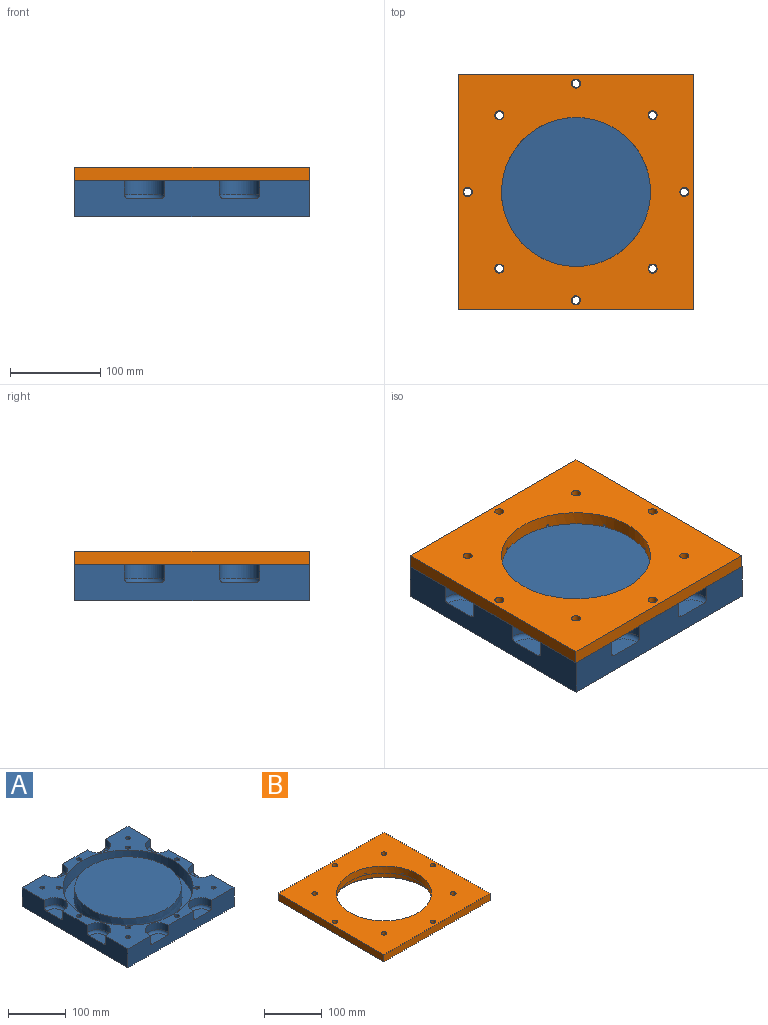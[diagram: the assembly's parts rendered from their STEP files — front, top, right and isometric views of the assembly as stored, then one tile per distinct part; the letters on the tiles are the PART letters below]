
ASSEMBLY  parts=2 mates=1
PART A: 46 faces, bbox 262x262x40 mm
  f0: plane 260x40mm, normal (0,1,0), area 8632.8mm2, adj f1,f15,f16,f17,f34,f35,f36,f37
  f1: plane 260x40mm, normal (-1,0,0), area 8632.8mm2, adj f0,f2,f16,f17,f30,f31,f32,f33
  f2: plane 260x40mm, normal (0,-1,0), area 8632.8mm2, adj f1,f15,f16,f17,f26,f27,f28,f29
  f3: cylinder r=4.3mm len=40mm, axis (0,0,1), area 1080.7mm2, adj f16,f17
  f4: cylinder r=4.3mm len=40mm, axis (0,0,1), area 1080.7mm2, adj f16,f17
  f5: cylinder r=4.3mm len=40mm, axis (0,0,1), area 1080.7mm2, adj f16,f17
  f6: cylinder r=4.3mm len=40mm, axis (0,0,1), area 1080.7mm2, adj f16,f17
  f7: cylinder r=4.3mm len=40mm, axis (0,0,1), area 1080.7mm2, adj f16,f17
  f8: cylinder r=4.3mm len=40mm, axis (0,0,1), area 1080.7mm2, adj f16,f17
  f9: cylinder r=4.3mm len=40mm, axis (0,0,1), area 1080.7mm2, adj f16,f17
  f10: cylinder r=4.3mm len=40mm, axis (0,0,1), area 1080.7mm2, adj f16,f17
  f11: cylinder r=4.3mm len=40mm, axis (0,0,1), area 1080.7mm2, adj f16,f17
  f12: cylinder r=4.3mm len=40mm, axis (0,0,1), area 1080.7mm2, adj f16,f17
  f13: cylinder r=4.3mm len=40mm, axis (0,0,1), area 1080.7mm2, adj f16,f17
  f14: cylinder r=4.3mm len=40mm, axis (0,0,1), area 1080.7mm2, adj f16,f17
  f15: plane 260x40mm, normal (1,0,0), area 8632.8mm2, adj f0,f2,f16,f17,f22,f23,f24,f25
  f16: plane 260x260mm, normal (0,0,-1), area 66902.9mm2, adj f0,f1,f2,f3,f4,f5,f6,f7
  f17: plane 260x260mm, normal (0,0,1), area 19526.4mm2, adj f0,f1,f2,f3,f4,f5,f6,f7
  f18: cone r=92.5mm half-angle=3deg, axis (0,0,-1), area 14652.8mm2, adj f20,f21
  f19: cone r=113mm half-angle=3deg, axis (0,0,1), area 17671.3mm2, adj f17,f20
  f20: plane 223.38x223.38mm, normal (0,0,1), area 11543mm2, adj f18,f19
  f21: plane 185x185mm, normal (0,0,1), area 26880.3mm2, adj f18
  f22: plane 35x20mm, normal (0,0,1), area 568.4mm2, adj f15,f43
  f23: cylinder r=22.5mm len=45mm, axis (0,0,1), area 1135.6mm2, adj f15,f17,f43
  f24: plane 35x20mm, normal (0,0,1), area 568.4mm2, adj f15,f42
  f25: cylinder r=22.5mm len=45mm, axis (0,0,1), area 1135.6mm2, adj f15,f17,f42
  f26: cylinder r=22.5mm len=45mm, axis (0,0,1), area 1135.6mm2, adj f2,f17,f45
  f27: plane 35x20mm, normal (0,0,1), area 568.4mm2, adj f2,f45
  f28: cylinder r=22.5mm len=45mm, axis (0,0,1), area 1135.6mm2, adj f2,f17,f44
  f29: plane 35x20mm, normal (0,0,1), area 568.4mm2, adj f2,f44
  f30: cylinder r=22.5mm len=45mm, axis (0,0,1), area 1135.6mm2, adj f1,f17,f39
  f31: plane 35x20mm, normal (0,0,1), area 568.4mm2, adj f1,f39
  f32: cylinder r=22.5mm len=45mm, axis (0,0,1), area 1135.6mm2, adj f1,f17,f38
  f33: plane 35x20mm, normal (0,0,1), area 568.4mm2, adj f1,f38
  f34: plane 35x20mm, normal (0,0,1), area 568.4mm2, adj f0,f41
  f35: cylinder r=22.5mm len=45mm, axis (0,0,1), area 1135.6mm2, adj f0,f17,f41
  f36: plane 35x20mm, normal (0,0,1), area 568.4mm2, adj f0,f40
  f37: cylinder r=22.5mm len=45mm, axis (0,0,1), area 1135.6mm2, adj f0,f17,f40
  f38: torus R=17.5mm, axis (0,0,1), area 549.8mm2, adj f1,f32,f33
  f39: torus R=17.5mm, axis (0,0,1), area 549.8mm2, adj f1,f30,f31
  f40: torus R=17.5mm, axis (0,0,1), area 549.8mm2, adj f0,f36,f37
  f41: torus R=17.5mm, axis (0,0,1), area 549.8mm2, adj f0,f34,f35
  f42: torus R=17.5mm, axis (0,0,1), area 549.8mm2, adj f15,f24,f25
  f43: torus R=17.5mm, axis (0,0,1), area 549.8mm2, adj f15,f22,f23
  f44: torus R=17.5mm, axis (0,0,1), area 549.8mm2, adj f2,f28,f29
  f45: torus R=17.5mm, axis (0,0,1), area 549.8mm2, adj f2,f26,f27
PART B: 152 faces, bbox 260x260x35 mm
  f0: plane 192.29x192.29mm, normal (0,0,-1), area 1974.4mm2, adj f24,f25,f26,f27,f28,f29,f30,f31
  f1: plane 260x260mm, normal (0,0,-1), area 26588.3mm2, adj f11,f12,f13,f14,f15,f16,f17,f18
  f2: plane 51.92x51.92mm, normal (0,0,-1), area 657.2mm2, adj f9,f36,f57,f61,f100,f101
  f3: plane 68.02x15.72mm, normal (0,0,-1), area 657.2mm2, adj f9,f38,f94,f95,f102,f103
  f4: plane 51.92x51.92mm, normal (0,0,-1), area 657.2mm2, adj f9,f24,f89,f90,f96,f97
  f5: plane 68.02x15.72mm, normal (0,0,-1), area 657.2mm2, adj f9,f26,f83,f84,f87,f91
  f6: plane 51.92x51.92mm, normal (0,0,-1), area 657.2mm2, adj f9,f28,f77,f78,f81,f85
  f7: plane 68.02x15.72mm, normal (0,0,-1), area 657.2mm2, adj f9,f30,f71,f72,f75,f79
  f8: plane 51.92x51.92mm, normal (0,0,-1), area 657.2mm2, adj f9,f32,f65,f66,f69,f73
  f9: cylinder r=82.5mm len=165mm, axis (0,0,-1), area 7703.4mm2, adj f2,f3,f4,f5,f6,f7,f8,f10
  f10: plane 68.02x15.72mm, normal (0,0,-1), area 657.2mm2, adj f9,f34,f59,f60,f63,f67
  f11: plane 260x15mm, normal (0,1,0), area 3900mm2, adj f1,f12,f14,f23
  f12: plane 260x15mm, normal (-1,0,0), area 3900mm2, adj f1,f11,f13,f23
  f13: plane 260x15mm, normal (0,-1,0), area 3900mm2, adj f1,f12,f14,f23
  f14: plane 260x15mm, normal (1,0,0), area 3900mm2, adj f1,f11,f13,f23
  f15: cylinder r=5mm len=15mm, axis (0,0,-1), area 471.2mm2, adj f1,f23
  f16: cylinder r=5mm len=15mm, axis (0,0,-1), area 471.2mm2, adj f1,f23
  f17: cylinder r=5mm len=15mm, axis (0,0,-1), area 471.2mm2, adj f1,f23
  f18: cylinder r=5mm len=15mm, axis (0,0,-1), area 471.2mm2, adj f1,f23
  f19: cylinder r=5mm len=15mm, axis (0,0,-1), area 471.2mm2, adj f1,f23
  f20: cylinder r=5mm len=15mm, axis (0,0,-1), area 471.2mm2, adj f1,f23
  f21: cylinder r=5mm len=15mm, axis (0,0,-1), area 471.2mm2, adj f1,f23
  f22: cylinder r=5mm len=15mm, axis (0,0,-1), area 471.2mm2, adj f1,f23
  f23: plane 260x260mm, normal (0,0,1), area 45589.2mm2, adj f9,f11,f12,f13,f14,f15,f16,f17
  f24: cone r=92.5mm half-angle=3deg, axis (0,0,-1), area 348mm2, adj f0,f4,f25,f55
  f25: cone r=1.5mm half-angle=3deg, axis (0,0,-1), area 24.5mm2, adj f0,f24,f26,f88
  f26: cone r=92.5mm half-angle=3deg, axis (0,0,-1), area 348mm2, adj f0,f5,f25,f27
  f27: cone r=1.5mm half-angle=3deg, axis (0,0,-1), area 24.5mm2, adj f0,f26,f28,f82
  f28: cone r=92.5mm half-angle=3deg, axis (0,0,-1), area 348mm2, adj f0,f6,f27,f29
  f29: cone r=1.5mm half-angle=3deg, axis (0,0,-1), area 24.5mm2, adj f0,f28,f30,f76
  f30: cone r=92.5mm half-angle=3deg, axis (0,0,-1), area 348mm2, adj f0,f7,f29,f31
  f31: cone r=1.5mm half-angle=3deg, axis (0,0,-1), area 24.5mm2, adj f0,f30,f32,f70
  f32: cone r=92.5mm half-angle=3deg, axis (0,0,-1), area 348mm2, adj f0,f8,f31,f33
  f33: cone r=1.5mm half-angle=3deg, axis (0,0,-1), area 24.5mm2, adj f0,f32,f34,f64
  f34: cone r=92.5mm half-angle=3deg, axis (0,0,-1), area 348mm2, adj f0,f10,f33,f35
  f35: cone r=1.5mm half-angle=3deg, axis (0,0,-1), area 24.5mm2, adj f0,f34,f36,f58
  f36: cone r=92.5mm half-angle=3deg, axis (0,0,-1), area 348mm2, adj f0,f2,f35,f37
  f37: cone r=1.5mm half-angle=3deg, axis (0,0,-1), area 24.5mm2, adj f0,f36,f38,f99
  f38: cone r=92.5mm half-angle=3deg, axis (0,0,-1), area 348mm2, adj f0,f3,f37,f55
  f39: cone r=1.5mm half-angle=3deg, axis (0,0,-1), area 24.3mm2, adj f40,f54,f56,f111
  f40: cone r=113mm half-angle=3deg, axis (0,0,1), area 427.6mm2, adj f1,f39,f41,f56
  f41: cone r=1.5mm half-angle=3deg, axis (0,0,-1), area 24.3mm2, adj f40,f42,f56,f106
  f42: cone r=113mm half-angle=3deg, axis (0,0,1), area 427.6mm2, adj f1,f41,f43,f56
  f43: cone r=1.5mm half-angle=3deg, axis (0,0,-1), area 24.3mm2, adj f42,f44,f56,f141
  f44: cone r=113mm half-angle=3deg, axis (0,0,1), area 427.6mm2, adj f1,f43,f45,f56
  f45: cone r=1.5mm half-angle=3deg, axis (0,0,-1), area 24.3mm2, adj f44,f46,f56,f136
  f46: cone r=113mm half-angle=3deg, axis (0,0,1), area 427.6mm2, adj f1,f45,f47,f56
  f47: cone r=1.5mm half-angle=3deg, axis (0,0,-1), area 24.3mm2, adj f46,f48,f56,f131
  f48: cone r=113mm half-angle=3deg, axis (0,0,1), area 427.6mm2, adj f1,f47,f49,f56
  f49: cone r=1.5mm half-angle=3deg, axis (0,0,-1), area 24.3mm2, adj f48,f50,f56,f126
  f50: cone r=113mm half-angle=3deg, axis (0,0,1), area 427.6mm2, adj f1,f49,f51,f56
  f51: cone r=1.5mm half-angle=3deg, axis (0,0,-1), area 24.3mm2, adj f50,f52,f56,f121
  f52: cone r=113mm half-angle=3deg, axis (0,0,1), area 427.6mm2, adj f1,f51,f53,f56
  f53: cone r=1.5mm half-angle=3deg, axis (0,0,-1), area 24.3mm2, adj f52,f54,f56,f116
  f54: cone r=113mm half-angle=3deg, axis (0,0,1), area 427.6mm2, adj f1,f39,f53,f56
  f55: cone r=1.5mm half-angle=3deg, axis (0,0,-1), area 24.5mm2, adj f0,f24,f38,f93
  f56: plane 225.48x225.48mm, normal (0,0,-1), area 2418.1mm2, adj f39,f40,f41,f42,f43,f44,f45,f46
  f57: plane 9.23x3.82mm, normal (0.38,0.92,0), area 30mm2, adj f2,f58,f61,f62
  f58: cylinder r=1.5mm len=3mm, axis (0,0,-1), area 14.2mm2, adj f35,f57,f59,f62
  f59: plane 9.23x3.82mm, normal (-0.38,-0.92,0), area 30mm2, adj f10,f58,f60,f62
  f60: cylinder r=1.5mm len=3mm, axis (0,0,-1), area 0mm2, adj f9,f10,f59,f62
  f61: cylinder r=1.5mm len=3mm, axis (0,0,-1), area 0mm2, adj f2,f9,f57,f62
  f62: plane 11.33x6.72mm, normal (0,0,-1), area 33.5mm2, adj f9,f57,f58,f59,f60,f61
  f63: plane 9.23x3.82mm, normal (-0.38,0.92,0), area 30mm2, adj f10,f64,f67,f68
  f64: cylinder r=1.5mm len=3mm, axis (0,0,-1), area 14.2mm2, adj f33,f63,f65,f68
  f65: plane 9.23x3.82mm, normal (0.38,-0.92,0), area 30mm2, adj f8,f64,f66,f68
  f66: cylinder r=1.5mm len=3mm, axis (0,0,-1), area 0mm2, adj f8,f9,f65,f68
  f67: cylinder r=1.5mm len=3mm, axis (0,0,-1), area 0mm2, adj f9,f10,f63,f68
  f68: plane 11.33x6.72mm, normal (0,0,-1), area 33.5mm2, adj f9,f63,f64,f65,f66,f67
  f69: plane 9.23x3.82mm, normal (-0.92,0.38,0), area 30mm2, adj f8,f70,f73,f74
  f70: cylinder r=1.5mm len=3mm, axis (0,0,-1), area 14.2mm2, adj f31,f69,f71,f74
  f71: plane 9.23x3.82mm, normal (0.92,-0.38,0), area 30mm2, adj f7,f70,f72,f74
  f72: cylinder r=1.5mm len=3mm, axis (0,0,-1), area 0mm2, adj f7,f9,f71,f74
  f73: cylinder r=1.5mm len=3mm, axis (0,0,-1), area 0mm2, adj f8,f9,f69,f74
  f74: plane 11.33x6.72mm, normal (0,0,-1), area 33.5mm2, adj f9,f69,f70,f71,f72,f73
  f75: plane 9.23x3.82mm, normal (-0.92,-0.38,0), area 30mm2, adj f7,f76,f79,f80
  f76: cylinder r=1.5mm len=3mm, axis (0,0,-1), area 14.2mm2, adj f29,f75,f77,f80
  f77: plane 9.23x3.82mm, normal (0.92,0.38,0), area 30mm2, adj f6,f76,f78,f80
  f78: cylinder r=1.5mm len=3mm, axis (0,0,-1), area 0mm2, adj f6,f9,f77,f80
  f79: cylinder r=1.5mm len=3mm, axis (0,0,-1), area 0mm2, adj f7,f9,f75,f80
  f80: plane 11.33x6.72mm, normal (0,0,-1), area 33.5mm2, adj f9,f75,f76,f77,f78,f79
  f81: plane 9.23x3.82mm, normal (-0.38,-0.92,0), area 30mm2, adj f6,f82,f85,f86
  f82: cylinder r=1.5mm len=3mm, axis (0,0,-1), area 14.2mm2, adj f27,f81,f83,f86
  f83: plane 9.23x3.82mm, normal (0.38,0.92,0), area 30mm2, adj f5,f82,f84,f86
  f84: cylinder r=1.5mm len=3mm, axis (0,0,-1), area 0mm2, adj f5,f9,f83,f86
  f85: cylinder r=1.5mm len=3mm, axis (0,0,-1), area 0mm2, adj f6,f9,f81,f86
  f86: plane 11.33x6.72mm, normal (0,0,-1), area 33.5mm2, adj f9,f81,f82,f83,f84,f85
  f87: plane 9.23x3.82mm, normal (0.38,-0.92,0), area 30mm2, adj f5,f88,f91,f92
  f88: cylinder r=1.5mm len=3mm, axis (0,0,-1), area 14.2mm2, adj f25,f87,f89,f92
  f89: plane 9.23x3.82mm, normal (-0.38,0.92,0), area 30mm2, adj f4,f88,f90,f92
  f90: cylinder r=1.5mm len=3mm, axis (0,0,-1), area 0mm2, adj f4,f9,f89,f92
  f91: cylinder r=1.5mm len=3mm, axis (0,0,-1), area 0mm2, adj f5,f9,f87,f92
  f92: plane 11.33x6.72mm, normal (0,0,-1), area 33.5mm2, adj f9,f87,f88,f89,f90,f91
  f93: cylinder r=1.5mm len=3mm, axis (0,0,-1), area 14.2mm2, adj f55,f94,f97,f98
  f94: plane 9.23x3.82mm, normal (-0.92,0.38,0), area 30mm2, adj f3,f93,f95,f98
  f95: cylinder r=1.5mm len=3mm, axis (0,0,-1), area 0mm2, adj f3,f9,f94,f98
  f96: cylinder r=1.5mm len=3mm, axis (0,0,-1), area 0mm2, adj f4,f9,f97,f98
  f97: plane 9.23x3.82mm, normal (0.92,-0.38,0), area 30mm2, adj f4,f93,f96,f98
  f98: plane 11.33x6.72mm, normal (0,0,-1), area 33.5mm2, adj f9,f93,f94,f95,f96,f97
  f99: cylinder r=1.5mm len=3mm, axis (0,0,-1), area 14.2mm2, adj f37,f100,f103,f104
  f100: plane 9.23x3.82mm, normal (-0.92,-0.38,0), area 30mm2, adj f2,f99,f101,f104
  f101: cylinder r=1.5mm len=3mm, axis (0,0,-1), area 0mm2, adj f2,f9,f100,f104
  f102: cylinder r=1.5mm len=3mm, axis (0,0,-1), area 0mm2, adj f3,f9,f103,f104
  f103: plane 9.23x3.82mm, normal (0.92,0.38,0), area 30mm2, adj f3,f99,f102,f104
  f104: plane 11.33x6.72mm, normal (0,0,-1), area 33.5mm2, adj f9,f99,f100,f101,f102,f103
  f105: plane 9.25x3.83mm, normal (-0.38,-0.92,0), area 30mm2, adj f1,f106,f108,f109
  f106: cylinder r=1.5mm len=3mm, axis (0,0,-1), area 14.1mm2, adj f1,f41,f105,f107,f109
  f107: plane 9.24x3.83mm, normal (0.38,0.92,0), area 30mm2, adj f1,f106,f108,f109
  f108: cylinder r=1.5mm len=3mm, axis (0,0,-1), area 14.1mm2, adj f1,f105,f107,f109
  f109: plane 12.24x6.83mm, normal (0,0,-1), area 37.1mm2, adj f105,f106,f107,f108
  f110: plane 9.25x3.83mm, normal (-0.92,-0.38,0), area 30mm2, adj f1,f111,f113,f114
  f111: cylinder r=1.5mm len=3mm, axis (0,0,-1), area 14.1mm2, adj f1,f39,f110,f112,f114
  f112: plane 9.24x3.83mm, normal (0.92,0.38,0), area 30mm2, adj f1,f111,f113,f114
  f113: cylinder r=1.5mm len=3mm, axis (0,0,-1), area 14.1mm2, adj f1,f110,f112,f114
  f114: plane 12.24x6.83mm, normal (0,0,-1), area 37.1mm2, adj f110,f111,f112,f113
  f115: plane 9.25x3.83mm, normal (-0.92,0.38,0), area 30mm2, adj f1,f116,f118,f119
  f116: cylinder r=1.5mm len=3mm, axis (0,0,-1), area 14.1mm2, adj f1,f53,f115,f117,f119
  f117: plane 9.24x3.83mm, normal (0.92,-0.38,0), area 30mm2, adj f1,f116,f118,f119
  f118: cylinder r=1.5mm len=3mm, axis (0,0,-1), area 14.1mm2, adj f1,f115,f117,f119
  f119: plane 12.24x6.83mm, normal (0,0,-1), area 37.1mm2, adj f115,f116,f117,f118
  f120: plane 9.25x3.83mm, normal (-0.38,0.92,0), area 30mm2, adj f1,f121,f123,f124
  f121: cylinder r=1.5mm len=3mm, axis (0,0,-1), area 14.1mm2, adj f1,f51,f120,f122,f124
  f122: plane 9.24x3.83mm, normal (0.38,-0.92,0), area 30mm2, adj f1,f121,f123,f124
  f123: cylinder r=1.5mm len=3mm, axis (0,0,-1), area 14.1mm2, adj f1,f120,f122,f124
  f124: plane 12.24x6.83mm, normal (0,0,-1), area 37.1mm2, adj f120,f121,f122,f123
  f125: plane 9.25x3.83mm, normal (0.38,0.92,0), area 30mm2, adj f1,f126,f128,f129
  f126: cylinder r=1.5mm len=3mm, axis (0,0,-1), area 14.1mm2, adj f1,f49,f125,f127,f129
  f127: plane 9.24x3.83mm, normal (-0.38,-0.92,0), area 30mm2, adj f1,f126,f128,f129
  f128: cylinder r=1.5mm len=3mm, axis (0,0,-1), area 14.1mm2, adj f1,f125,f127,f129
  f129: plane 12.24x6.83mm, normal (0,0,-1), area 37.1mm2, adj f125,f126,f127,f128
  f130: plane 9.25x3.83mm, normal (0.92,0.38,0), area 30mm2, adj f1,f131,f133,f134
  f131: cylinder r=1.5mm len=3mm, axis (0,0,-1), area 14.1mm2, adj f1,f47,f130,f132,f134
  f132: plane 9.24x3.83mm, normal (-0.92,-0.38,0), area 30mm2, adj f1,f131,f133,f134
  f133: cylinder r=1.5mm len=3mm, axis (0,0,-1), area 14.1mm2, adj f1,f130,f132,f134
  f134: plane 12.24x6.83mm, normal (0,0,-1), area 37.1mm2, adj f130,f131,f132,f133
  f135: plane 9.25x3.83mm, normal (0.92,-0.38,0), area 30mm2, adj f1,f136,f138,f139
  f136: cylinder r=1.5mm len=3mm, axis (0,0,-1), area 14.1mm2, adj f1,f45,f135,f137,f139
  f137: plane 9.24x3.83mm, normal (-0.92,0.38,0), area 30mm2, adj f1,f136,f138,f139
  f138: cylinder r=1.5mm len=3mm, axis (0,0,-1), area 14.1mm2, adj f1,f135,f137,f139
  f139: plane 12.24x6.83mm, normal (0,0,-1), area 37.1mm2, adj f135,f136,f137,f138
  f140: plane 9.25x3.83mm, normal (0.38,-0.92,0), area 30mm2, adj f1,f141,f143,f144
  f141: cylinder r=1.5mm len=3mm, axis (0,0,-1), area 14.1mm2, adj f1,f43,f140,f142,f144
  f142: plane 9.24x3.83mm, normal (-0.38,0.92,0), area 30mm2, adj f1,f141,f143,f144
  f143: cylinder r=1.5mm len=3mm, axis (0,0,-1), area 14.1mm2, adj f1,f140,f142,f144
  f144: plane 12.24x6.83mm, normal (0,0,-1), area 37.1mm2, adj f140,f141,f142,f143
  f145: cylinder r=97.14mm len=194.29mm, axis (0,0,1), area 7934.7mm2, adj f149,f150
  f146: cylinder r=108.23mm len=216.45mm, axis (0,0,1), area 8840mm2, adj f148,f151
  f147: plane 214.45x214.45mm, normal (0,0,-1), area 5859.9mm2, adj f150,f151
  f148: torus R=109.23mm, axis (0,0,1), area 1071.7mm2, adj f56,f146
  f149: torus R=96.14mm, axis (0,0,1), area 955.2mm2, adj f0,f145
  f150: torus R=98.14mm, axis (0,0,1), area 962.3mm2, adj f145,f147
  f151: torus R=107.22mm, axis (0,0,1), area 1064.6mm2, adj f146,f147
PLACE A t=(1.24,-0.02,0)mm
PLACE B at identity
MATE fastened A.f3 <-> B.f22  axis (0,0,1) through (121.24,-0.02,0)mm
